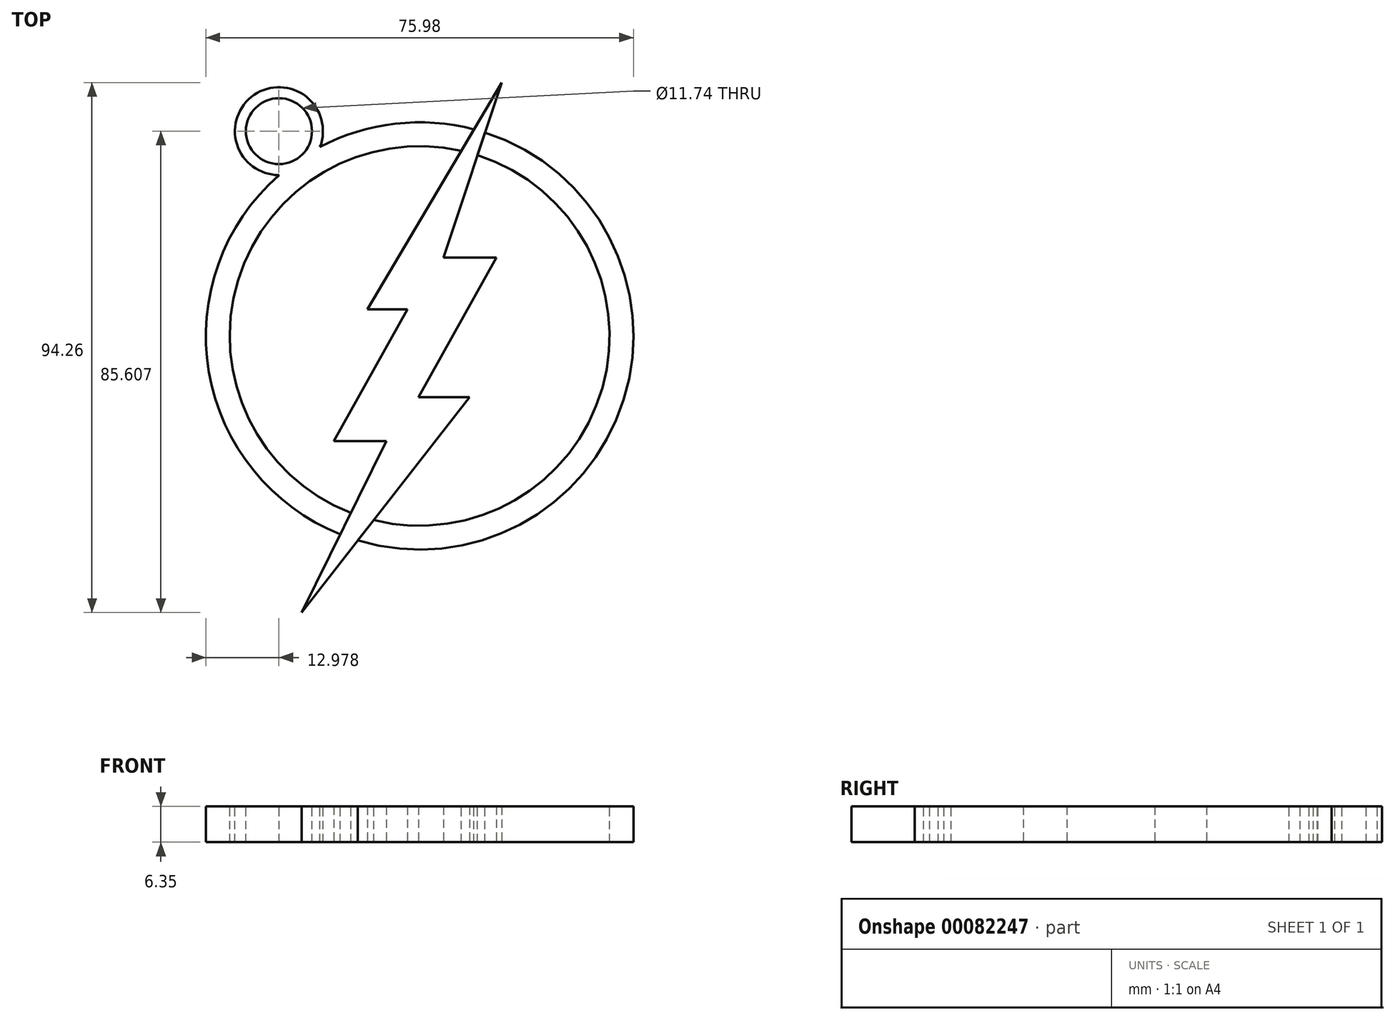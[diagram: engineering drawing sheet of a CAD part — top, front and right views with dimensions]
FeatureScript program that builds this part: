
annotation { "Feature Type Name" : "Feature", "Feature Type Description" : "" }
export const myFeature = defineFeature(function(context is Context, id is Id, definition is map)
    precondition{}
    {
        {
            var Q0;
            Q0=qCreatedBy(makeId("Top.planeOp"),FACE);
            var sketch = newSketch(context, id + "F0", { "sketchPlane" : qUnion([Q0])});
            skLineSegment(sketch, "E0", {"start": v(20.53, 51.39) * mm, "end": v(-3.33, 11.02) * mm});
            skLineSegment(sketch, "E1", {"start": v(-3.33, 11.02) * mm, "end": v(3.78, 11.02) * mm});
            skLineSegment(sketch, "E2", {"start": v(3.78, 11.02) * mm, "end": v(-9.3, -12.37) * mm});
            skLineSegment(sketch, "E3", {"start": v(-9.3, -12.37) * mm, "end": v(0, -12.37) * mm});
            skLineSegment(sketch, "E4", {"start": v(0, -12.37) * mm, "end": v(-15.02, -42.87) * mm});
            skLineSegment(sketch, "E5", {"start": v(-15.02, -42.87) * mm, "end": v(14.8, -4.57) * mm});
            skLineSegment(sketch, "E6", {"start": v(14.8, -4.57) * mm, "end": v(5.75, -4.57) * mm});
            skLineSegment(sketch, "E7", {"start": v(5.75, -4.57) * mm, "end": v(19.61, 20.24) * mm});
            skLineSegment(sketch, "E8", {"start": v(19.61, 20.24) * mm, "end": v(10.2, 20.24) * mm});
            skLineSegment(sketch, "E9", {"start": v(20.53, 51.39) * mm, "end": v(10.2, 20.24) * mm});
            skSolve(sketch);
        }
        {
            var Q0;
            Q0 = qSketchRegion(id + "F0", true);
            extrude(context, id + "F1", {"entities" : qUnion([Q0]), "depth" : 6.35 * mm});
        }
        {
            var Q0;
            Q0=makeQuery(id+"F1.opExtrude","CAP_FACE",FACE,{"disambiguationData":[OSD([sQuery(id+"F0.wireOp",EDGE,"E0"),sQuery(id+"F0.wireOp",EDGE,"E1"),sQuery(id+"F0.wireOp",EDGE,"E2"),sQuery(id+"F0.wireOp",EDGE,"E3"),sQuery(id+"F0.wireOp",EDGE,"E4"),sQuery(id+"F0.wireOp",EDGE,"E5"),sQuery(id+"F0.wireOp",EDGE,"E6"),sQuery(id+"F0.wireOp",EDGE,"E7"),sQuery(id+"F0.wireOp",EDGE,"E8"),sQuery(id+"F0.wireOp",EDGE,"E9")])],"isStart":false});
            var sketch = newSketch(context, id + "F2", { "sketchPlane" : qUnion([Q0])});
            skCircle(sketch, "E10", {"center": v(5.95, 6.31) * mm, "radius": 33.75 * mm});
            skCircle(sketch, "E11", {"center": v(5.95, 6.31) * mm, "radius": 38 * mm});
            skSolve(sketch);
        }
        {
            var Q0;
            {var subQ0=sQuery(id+"F2.wireOp",EDGE,"E10");var subQ1=makeQuery(id+"F1.opExtrude","CAP_EDGE",EDGE,{"disambiguationData":[OSD([sQuery(id+"F0.wireOp",EDGE,"E0")])],"isStart":false});var subQ2=makeQuery(id+"F2.imprint","INTERSECT",VERTEX,{"derivedFrom":[subQ1,subQ0]});Q0=makeQuery(id+"F2.imprint","IMPRINT",FACE,{"disambiguationData":[TD([[makeQuery(id+"F2.imprint","IMPRINT",EDGE,{"disambiguationData":[TD([[subQ2,-1.0]])],"derivedFrom":subQ0}),-1.0]])]});}
            var Q1;
            {var subQ0=sQuery(id+"F2.wireOp",EDGE,"E10");var subQ1=makeQuery(id+"F1.opExtrude","CAP_EDGE",EDGE,{"disambiguationData":[OSD([sQuery(id+"F0.wireOp",EDGE,"E9")])],"isStart":false});var subQ2=makeQuery(id+"F2.imprint","INTERSECT",VERTEX,{"derivedFrom":[subQ1,subQ0]});Q1=makeQuery(id+"F2.imprint","IMPRINT",FACE,{"disambiguationData":[TD([[makeQuery(id+"F2.imprint","IMPRINT",EDGE,{"disambiguationData":[TD([[subQ2,1.0]])],"derivedFrom":subQ0}),-1.0]])]});}
            extrude(context, id + "F3", {"entities" : qUnion([Q0, Q1]), "oppositeDirection" : true, "depth" : 6.35 * mm});
        }
        {
            var Q0;
            Q0=makeQuery(id+"F1.opExtrude","CAP_FACE",FACE,{"disambiguationData":[OSD([sQuery(id+"F0.wireOp",EDGE,"E0"),sQuery(id+"F0.wireOp",EDGE,"E1"),sQuery(id+"F0.wireOp",EDGE,"E2"),sQuery(id+"F0.wireOp",EDGE,"E3"),sQuery(id+"F0.wireOp",EDGE,"E4"),sQuery(id+"F0.wireOp",EDGE,"E5"),sQuery(id+"F0.wireOp",EDGE,"E6"),sQuery(id+"F0.wireOp",EDGE,"E7"),sQuery(id+"F0.wireOp",EDGE,"E8"),sQuery(id+"F0.wireOp",EDGE,"E9")])],"isStart":false});
            var sketch = newSketch(context, id + "F4", { "sketchPlane" : qUnion([Q0])});
            skCircle(sketch, "E12", {"center": v(-19.06, 42.74) * mm, "radius": 7.82 * mm});
            skCircle(sketch, "E13", {"center": v(-19.06, 42.74) * mm, "radius": 5.87 * mm});
            skSolve(sketch);
        }
        {
            var Q0;
            Q0 = qSketchRegion(id + "F4", true);
            extrude(context, id + "F5", {"entities" : qUnion([Q0]), "operationType" : NewBodyOperationType.ADD, "oppositeDirection" : true, "depth" : 6.35 * mm});
        }
    });
